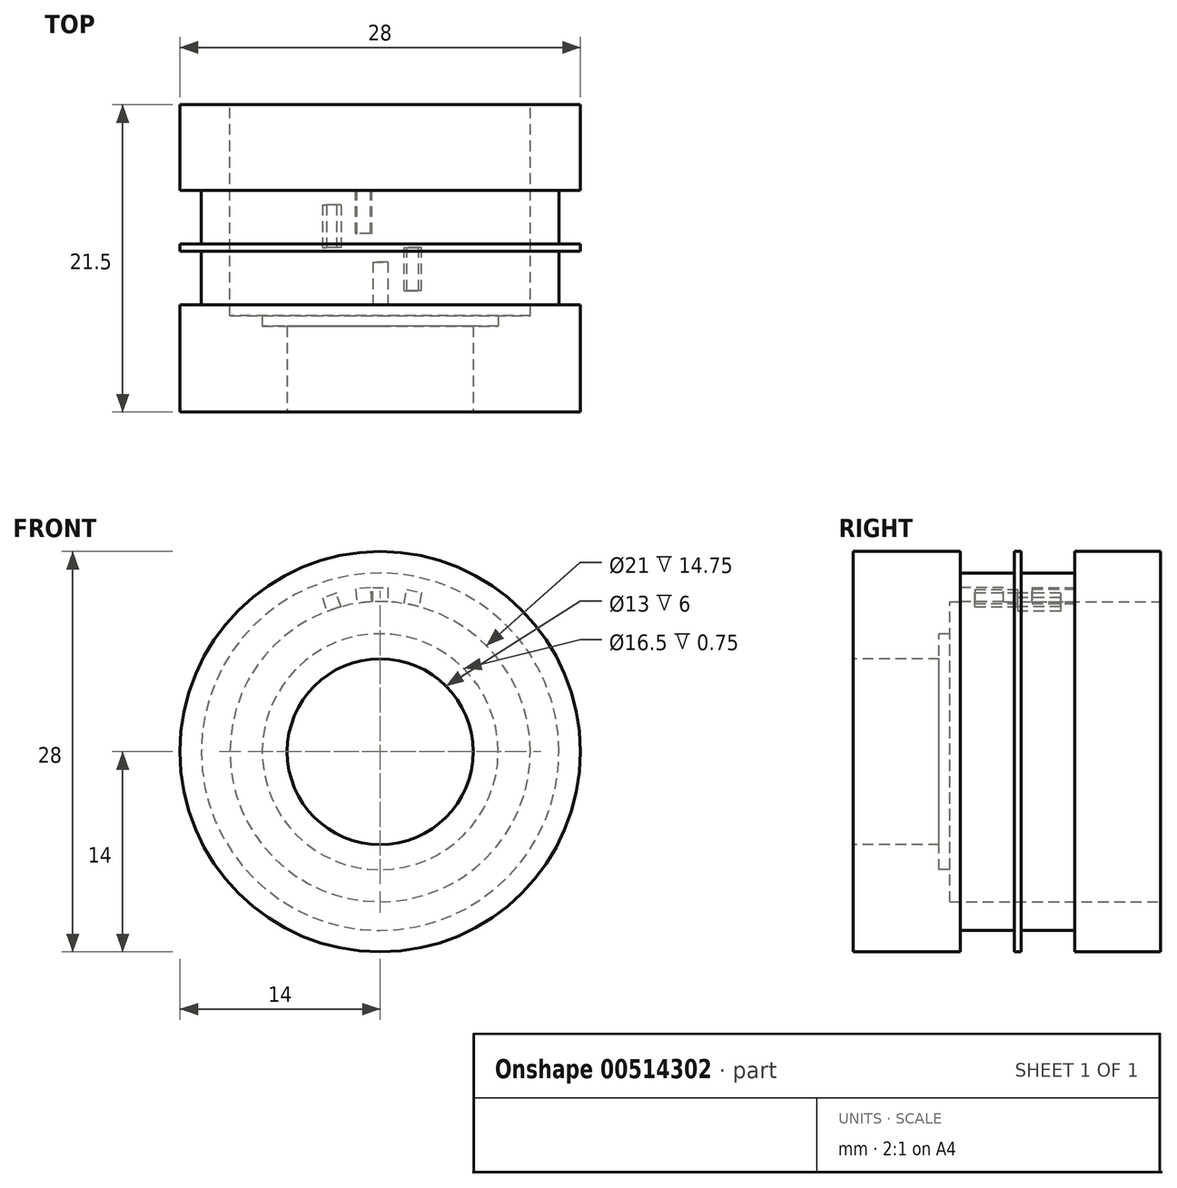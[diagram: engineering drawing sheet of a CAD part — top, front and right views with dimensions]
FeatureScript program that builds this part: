
annotation { "Feature Type Name" : "Feature", "Feature Type Description" : "" }
export const myFeature = defineFeature(function(context is Context, id is Id, definition is map)
    precondition{}
    {
        {
            var Q0;
            Q0=qCreatedBy(makeId("Front.planeOp"),FACE);
            var sketch = newSketch(context, id + "F0", { "sketchPlane" : qUnion([Q0])});
            skCircle(sketch, "E0", {"center": v(0, 0) * mm, "radius": 12.5 * mm});
            skCircle(sketch, "E1", {"center": v(0, 0) * mm, "radius": 10.5 * mm});
            skSolve(sketch);
        }
        {
            var Q0;
            Q0=makeQuery(id+"F0.imprint","IMPRINT",FACE,{"disambiguationData":[TD([[makeQuery(id+"F0.imprint","IMPRINT",EDGE,{"derivedFrom":sQuery(id+"F0.wireOp",EDGE,"E0")}),1.0]])]});
            extrude(context, id + "F1", {"entities" : qUnion([Q0]), "depth" : 8 * mm, "offsetDistance" : 25 * mm, "symmetric" : true});
        }
        {
            var Q0;
            Q0=makeQuery(id+"F1.opExtrude","CAP_FACE",FACE,{"disambiguationData":[OSD([sQuery(id+"F0.wireOp",EDGE,"E0"),sQuery(id+"F0.wireOp",EDGE,"E1")])],"isStart":false});
            var sketch = newSketch(context, id + "F2", { "sketchPlane" : qUnion([Q0])});
            skLineSegment(sketch, "E2", {"start": v(-0.53, 10.49) * mm, "end": v(-0.53, 11.49) * mm});
            skLineSegment(sketch, "E3", {"start": v(-0.53, 11.49) * mm, "end": v(0.53, 11.49) * mm});
            skLineSegment(sketch, "E4", {"start": v(0.52, 11.49) * mm, "end": v(0.52, 10.49) * mm});
            skSolve(sketch);
        }
        {
            var Q0;
            {var subQ0=sQuery(id+"F2.wireOp",EDGE,"E2");Q0=makeQuery(id+"F2.imprint","IMPRINT",FACE,{"disambiguationData":[TD([[makeQuery(id+"F2.imprint","IMPRINT",EDGE,{"derivedFrom":subQ0}),-1.0]])]});}
            extrude(context, id + "F3", {"entities" : qUnion([Q0]), "operationType" : NewBodyOperationType.REMOVE, "oppositeDirection" : true, "depth" : 3 * mm, "offsetDistance" : 25 * mm});
        }
        {
            var Q0;
            Q0=makeQuery(id+"F1.opExtrude","CAP_FACE",FACE,{"disambiguationData":[OSD([sQuery(id+"F0.wireOp",EDGE,"E0"),sQuery(id+"F0.wireOp",EDGE,"E1")])],"isStart":true});
            var sketch = newSketch(context, id + "F4", { "sketchPlane" : qUnion([Q0])});
            skLineSegment(sketch, "E5", {"start": v(0, 0) * mm, "end": v(1.03, 9.81) * mm, "construction": true});
            skLineSegment(sketch, "E6", {"start": v(0.57, 10.48) * mm, "end": v(0.68, 11.48) * mm});
            skLineSegment(sketch, "E7", {"start": v(0.68, 11.48) * mm, "end": v(1.72, 11.37) * mm});
            skLineSegment(sketch, "E8", {"start": v(1.72, 11.37) * mm, "end": v(1.62, 10.37) * mm});
            skSolve(sketch);
        }
        {
            var Q0;
            {var subQ0=sQuery(id+"F4.wireOp",EDGE,"E6");Q0=makeQuery(id+"F4.imprint","IMPRINT",FACE,{"disambiguationData":[TD([[makeQuery(id+"F4.imprint","IMPRINT",EDGE,{"derivedFrom":subQ0}),-1.0]])]});}
            extrude(context, id + "F5", {"entities" : qUnion([Q0]), "operationType" : NewBodyOperationType.REMOVE, "oppositeDirection" : true, "depth" : 3 * mm, "offsetDistance" : 25 * mm});
        }
        {
            var Q0;
            Q0=qCreatedBy(makeId("Front.planeOp"),FACE);
            var sketch = newSketch(context, id + "F6", { "sketchPlane" : qUnion([Q0])});
            skLineSegment(sketch, "E9", {"start": v(0, 0) * mm, "end": v(2.37, 11.14) * mm, "construction": true});
            skArc(sketch, "E10", {"start": v(2.7, 10.15) * mm, "mid": v(2.18, 10.27) * mm, "end": v(1.67, 10.37) * mm, "construction": true});
            skLineSegment(sketch, "E11", {"start": v(1.67, 10.37) * mm, "end": v(1.87, 11.35) * mm});
            skLineSegment(sketch, "E12", {"start": v(1.87, 11.35) * mm, "end": v(2.9, 11.13) * mm});
            skLineSegment(sketch, "E13", {"start": v(2.9, 11.13) * mm, "end": v(2.7, 10.15) * mm});
            skArc(sketch, "E14", {"start": v(2.7, 10.15) * mm, "mid": v(2.18, 10.27) * mm, "end": v(1.67, 10.37) * mm});
            skSolve(sketch);
        }
        {
            var Q0;
            Q0 = qSketchRegion(id + "F6", true);
            extrude(context, id + "F7", {"entities" : qUnion([Q0]), "operationType" : NewBodyOperationType.REMOVE, "depth" : 3 * mm, "offsetDistance" : 25 * mm});
        }
        {
            var Q0;
            Q0=qCreatedBy(makeId("Front.planeOp"),FACE);
            var sketch = newSketch(context, id + "F8", { "sketchPlane" : qUnion([Q0])});
            skLineSegment(sketch, "E15", {"start": v(0, 0) * mm, "end": v(-5.55, 17.07) * mm, "construction": true});
            skArc(sketch, "E16", {"start": v(-2.74, 10.14) * mm, "mid": v(-3.24, 9.99) * mm, "end": v(-3.74, 9.81) * mm});
            skLineSegment(sketch, "E17", {"start": v(-2.74, 10.14) * mm, "end": v(-3.05, 11.09) * mm});
            skLineSegment(sketch, "E18", {"start": v(-3.05, 11.09) * mm, "end": v(-4.05, 10.76) * mm});
            skLineSegment(sketch, "E19", {"start": v(-4.05, 10.76) * mm, "end": v(-3.74, 9.81) * mm});
            skSolve(sketch);
        }
        {
            var Q0;
            Q0 = qSketchRegion(id + "F8", true);
            extrude(context, id + "F9", {"entities" : qUnion([Q0]), "operationType" : NewBodyOperationType.REMOVE, "oppositeDirection" : true, "depth" : 3 * mm, "offsetDistance" : 25 * mm});
        }
        {
            var Q0;
            Q0=qCreatedBy(makeId("Right.planeOp"),FACE);
            var sketch = newSketch(context, id + "F10", { "sketchPlane" : qUnion([Q0])});
            skLineSegment(sketch, "E20", {"start": v(-11.5, 14) * mm, "end": v(-4, 14) * mm});
            skLineSegment(sketch, "E21", {"start": v(-4, 14) * mm, "end": v(-4, 10.5) * mm});
            skLineSegment(sketch, "E22", {"start": v(4, 10.5) * mm, "end": v(4, 14) * mm});
            skLineSegment(sketch, "E23", {"start": v(4, 14) * mm, "end": v(10, 14) * mm});
            skLineSegment(sketch, "E24", {"start": v(10, 14) * mm, "end": v(10, 10.5) * mm});
            skLineSegment(sketch, "E25", {"start": v(10, 10.5) * mm, "end": v(4, 10.5) * mm});
            skLineSegment(sketch, "E26", {"start": v(0.25, 14) * mm, "end": v(0.25, 12.5) * mm});
            skLineSegment(sketch, "E27", {"start": v(0.25, 12.5) * mm, "end": v(-0.25, 12.5) * mm});
            skLineSegment(sketch, "E28", {"start": v(-0.25, 12.5) * mm, "end": v(-0.25, 14) * mm});
            skPoint(sketch, "E29.end.orphan", {"position": v(0, 14) * mm});
            skLineSegment(sketch, "E30", {"start": v(-0.25, 14) * mm, "end": v(0.25, 14) * mm});
            skPoint(sketch, "E31.orphan", {"position": v(-16, 0) * mm});
            skPoint(sketch, "E32.orphan", {"position": v(-4, 0) * mm});
            skPoint(sketch, "E33.orphan", {"position": v(-11.5, 6.5) * mm});
            skPoint(sketch, "E34.start.orphan", {"position": v(-14.25, 6.5) * mm});
            skLineSegment(sketch, "E35", {"start": v(-11.5, 6.5) * mm, "end": v(-11.5, 14) * mm});
            skLineSegment(sketch, "E36", {"start": v(-11.5, 6.5) * mm, "end": v(-5.5, 6.5) * mm});
            skLineSegment(sketch, "E37", {"start": v(-4.75, 8.25) * mm, "end": v(-5.5, 8.25) * mm});
            skLineSegment(sketch, "E38", {"start": v(-5.5, 8.25) * mm, "end": v(-5.5, 6.5) * mm});
            skLineSegment(sketch, "E39", {"start": v(-4, 10.5) * mm, "end": v(-4.75, 10.5) * mm});
            skLineSegment(sketch, "E40", {"start": v(-4.75, 10.5) * mm, "end": v(-4.75, 8.25) * mm});
            skSolve(sketch);
        }
        {
            var Q0;
            Q0 = qSketchRegion(id + "F10", true);
            var Q1;
            Q1=makeQuery(id+"F1.opExtrude","SWEPT_FACE",FACE,{"disambiguationData":[OSD([sQuery(id+"F0.wireOp",EDGE,"E0")])]});
            revolve(context, id + "F11", {"operationType" : NewBodyOperationType.ADD, "entities" : qUnion([Q0]), "axis" : qUnion([Q1]), "revolveType" : RevolveType.FULL});
        }
    });
